# Revit family: Nivellierbare Kassette für Revisionsöffnung_ Montagedeckel_für_Zugdose_UKL
name_source: partatom
category: Generic Models
revit_build: Autodesk Revit 2015 (Build: 20140606_1530(x64)
units: mm (PartAtom-declared; Revit-internal decimal feet)

## types (2) — shared parameters
Manufacturer = OBO Bettermann
Material = Steel, Galvanized
URL = http://www.obo-bettermann.com

## per-type parameters (varying)
| type | "A" Dimension | "B" Dimension | GTIN | Height | Manufacturer Art.No. | Size "a" | Size "b" | Width | Width 2 |
| DUG UKL8 | 260 mm  [stored 0.853018 ft] | 380 mm  [stored 1.24672 ft] | 4012196436125 | 14 mm  [stored 0.0459318 ft] | 7428540 | 161 mm | 283 mm | 250 mm  [stored 0.82021 ft] | 123 mm |
| DUG UKL4 | 230 mm  [stored 0.754593 ft] | 370 mm  [stored 1.21391 ft] | 4012195709848 | 13 mm | 7428538 | 131 mm | 271 mm | 235 mm  [stored 0.770997 ft] | 89 mm |

note: column(s) folded — value = type name in every type: Article Type

note: [stored X ft] marks values corroborated as IEEE doubles in the binary element streams (Revit-internal decimal feet)

## geometry (parser evidence)
native form markers: Sweep x2
no freeform markers — native parametric forms only
